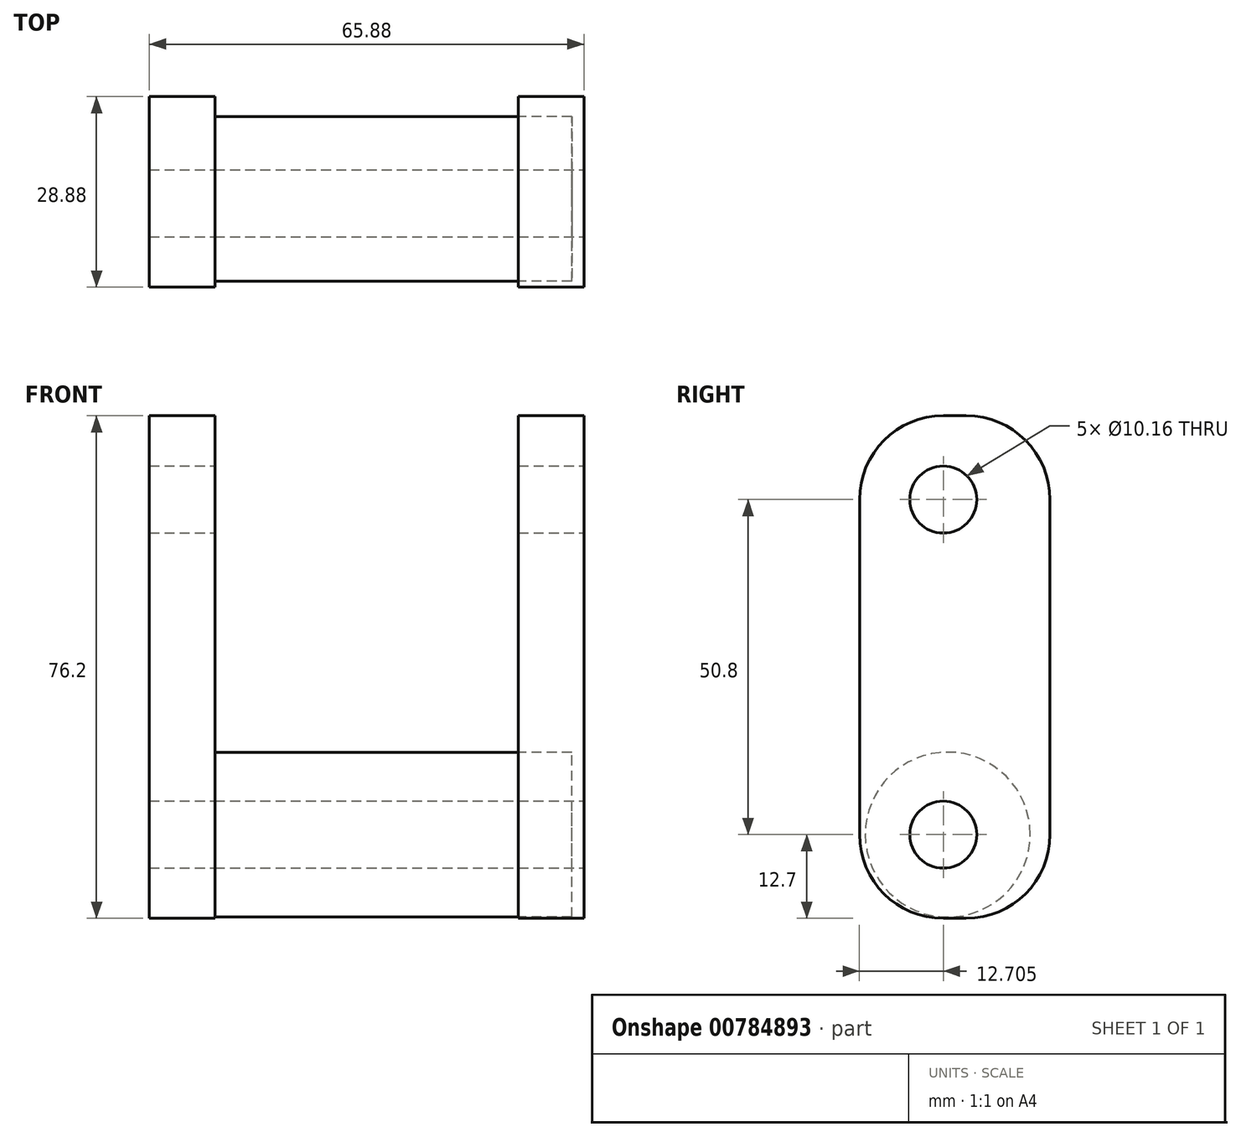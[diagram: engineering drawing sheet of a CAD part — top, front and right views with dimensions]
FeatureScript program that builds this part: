
annotation { "Feature Type Name" : "Feature", "Feature Type Description" : "" }
export const myFeature = defineFeature(function(context is Context, id is Id, definition is map)
    precondition{}
    {
        {
            var Q0;
            Q0=qCreatedBy(makeId("Top.planeOp"),FACE);
            var sketch = newSketch(context, id + "F0", { "sketchPlane" : qUnion([Q0])});
            skLineSegment(sketch, "E0.bottom", {"start": v(-32.94, 15.5) * mm, "end": v(-23.01, 15.5) * mm});
            skLineSegment(sketch, "E0.top", {"start": v(-32.94, -13.39) * mm, "end": v(-23.01, -13.39) * mm});
            skLineSegment(sketch, "E0.left", {"start": v(-32.94, 15.5) * mm, "end": v(-32.94, -13.39) * mm});
            skLineSegment(sketch, "E0.right", {"start": v(-23.01, 15.5) * mm, "end": v(-23.01, -13.39) * mm});
            skLineSegment(sketch, "E1.MirrorCS", {"start": v(32.94, 15.5) * mm, "end": v(23.01, 15.5) * mm});
            skLineSegment(sketch, "E2.MirrorCS", {"start": v(32.94, -13.39) * mm, "end": v(23.01, -13.39) * mm});
            skLineSegment(sketch, "E3.MirrorCS", {"start": v(32.94, 15.5) * mm, "end": v(32.94, -13.39) * mm});
            skLineSegment(sketch, "E4.MirrorCS", {"start": v(23.01, 15.5) * mm, "end": v(23.01, -13.39) * mm});
            skSolve(sketch);
        }
        {
            var Q0;
            Q0=makeQuery(id+"F0.imprint","IMPRINT",FACE,{"disambiguationData":[TD([[makeQuery(id+"F0.imprint","IMPRINT",EDGE,{"derivedFrom":sQuery(id+"F0.wireOp",EDGE,"E0.bottom")}),-1.0]])]});
            var Q1;
            Q1=makeQuery(id+"F0.imprint","IMPRINT",FACE,{"disambiguationData":[TD([[makeQuery(id+"F0.imprint","IMPRINT",EDGE,{"derivedFrom":sQuery(id+"F0.wireOp",EDGE,"E1.MirrorCS")}),1.0]])]});
            extrude(context, id + "F1", {"entities" : qUnion([Q0, Q1]), "depth" : 76.2 * mm, "offsetDistance" : 25.4 * mm});
        }
        {
            var Q0;
            Q0=makeQuery(id+"F1.opExtrude","CAP_EDGE",EDGE,{"disambiguationData":[OSD([sQuery(id+"F0.wireOp",EDGE,"E0.bottom")])],"isStart":false});
            var Q1;
            Q1=makeQuery(id+"F1.opExtrude","CAP_EDGE",EDGE,{"disambiguationData":[OSD([sQuery(id+"F0.wireOp",EDGE,"E0.top")])],"isStart":false});
            var Q2;
            Q2=makeQuery(id+"F1.opExtrude","CAP_EDGE",EDGE,{"disambiguationData":[OSD([sQuery(id+"F0.wireOp",EDGE,"E1.MirrorCS")])],"isStart":false});
            var Q3;
            Q3=makeQuery(id+"F1.opExtrude","CAP_EDGE",EDGE,{"disambiguationData":[OSD([sQuery(id+"F0.wireOp",EDGE,"E2.MirrorCS")])],"isStart":false});
            var Q4;
            Q4=makeQuery(id+"F1.opExtrude","CAP_EDGE",EDGE,{"disambiguationData":[OSD([sQuery(id+"F0.wireOp",EDGE,"E2.MirrorCS")])],"isStart":true});
            var Q5;
            Q5=makeQuery(id+"F1.opExtrude","CAP_EDGE",EDGE,{"disambiguationData":[OSD([sQuery(id+"F0.wireOp",EDGE,"E0.top")])],"isStart":true});
            var Q6;
            Q6=makeQuery(id+"F1.opExtrude","CAP_EDGE",EDGE,{"disambiguationData":[OSD([sQuery(id+"F0.wireOp",EDGE,"E0.bottom")])],"isStart":true});
            var Q7;
            Q7=makeQuery(id+"F1.opExtrude","CAP_EDGE",EDGE,{"disambiguationData":[OSD([sQuery(id+"F0.wireOp",EDGE,"E1.MirrorCS")])],"isStart":true});
            fillet(context, id + "F2", {"entities" : qUnion([Q0, Q1, Q2, Q3, Q4, Q5, Q6, Q7]), "radius" : 12.7 * mm, "tangentPropagation" : true, "allowEdgeOverflow" : false});
        }
        {
            var Q0;
            Q0=makeQuery(id+"F1.opExtrude","SWEPT_FACE",FACE,{"disambiguationData":[OSD([sQuery(id+"F0.wireOp",EDGE,"E0.right")])]});
            var sketch = newSketch(context, id + "F3", { "sketchPlane" : qUnion([Q0])});
            skCircle(sketch, "E5", {"center": v(0, 12.7) * mm, "radius": 12.5 * mm});
            skSolve(sketch);
        }
        {
            var Q0;
            Q0 = qSketchRegion(id + "F3", true);
            extrude(context, id + "F4", {"entities" : qUnion([Q0]), "depth" : 54.1 * mm, "offsetDistance" : 25.4 * mm});
        }
        {
            var Q0;
            Q0=makeQuery(id+"F1.opExtrude","SWEPT_FACE",FACE,{"disambiguationData":[OSD([sQuery(id+"F0.wireOp",EDGE,"E3.MirrorCS")])]});
            var sketch = newSketch(context, id + "F5", { "sketchPlane" : qUnion([Q0])});
            skCircle(sketch, "E6", {"center": v(-0.69, 12.7) * mm, "radius": 4.48 * mm});
            skCircle(sketch, "E7", {"center": v(-0.69, 63.5) * mm, "radius": 4.4 * mm});
            skSolve(sketch);
        }
        {
            var Q0;
            Q0=sQuery(id+"F5.wireOp",VERTEX,"E6.center");
            var Q1;
            Q1=sQuery(id+"F5.wireOp",VERTEX,"E7.center");
            var Q2;
            Q2=makeQuery(id+"F1.opExtrude","SWEPT_BODY",BODY,{"disambiguationData":[OSD([sQuery(id+"F0.wireOp",EDGE,"E0.bottom"),sQuery(id+"F0.wireOp",EDGE,"E0.top"),sQuery(id+"F0.wireOp",EDGE,"E0.left"),sQuery(id+"F0.wireOp",EDGE,"E0.right")])]});
            var Q3;
            Q3=makeQuery(id+"F1.opExtrude","SWEPT_BODY",BODY,{"disambiguationData":[OSD([sQuery(id+"F0.wireOp",EDGE,"E1.MirrorCS"),sQuery(id+"F0.wireOp",EDGE,"E2.MirrorCS"),sQuery(id+"F0.wireOp",EDGE,"E3.MirrorCS"),sQuery(id+"F0.wireOp",EDGE,"E4.MirrorCS")])]});
            var Q4;
            Q4=makeQuery(id+"F4.opExtrude","SWEPT_BODY",BODY,{"disambiguationData":[OSD([sQuery(id+"F3.wireOp",EDGE,"E5")])]});
            hole(context, id + "F6", {"style" : HoleStyle.SIMPLE, "endStyle" : HoleEndStyle.THROUGH, "holeDiameter" : 10.16 * mm, "majorDiameter" : 6.35 * mm, "isTappedThrough" : true, "tappedDepth" : 12.7 * mm, "tapClearance" : 3, "locations" : qUnion([Q0, Q1]), "scope" : qUnion([Q2, Q3, Q4])});
        }
    });
